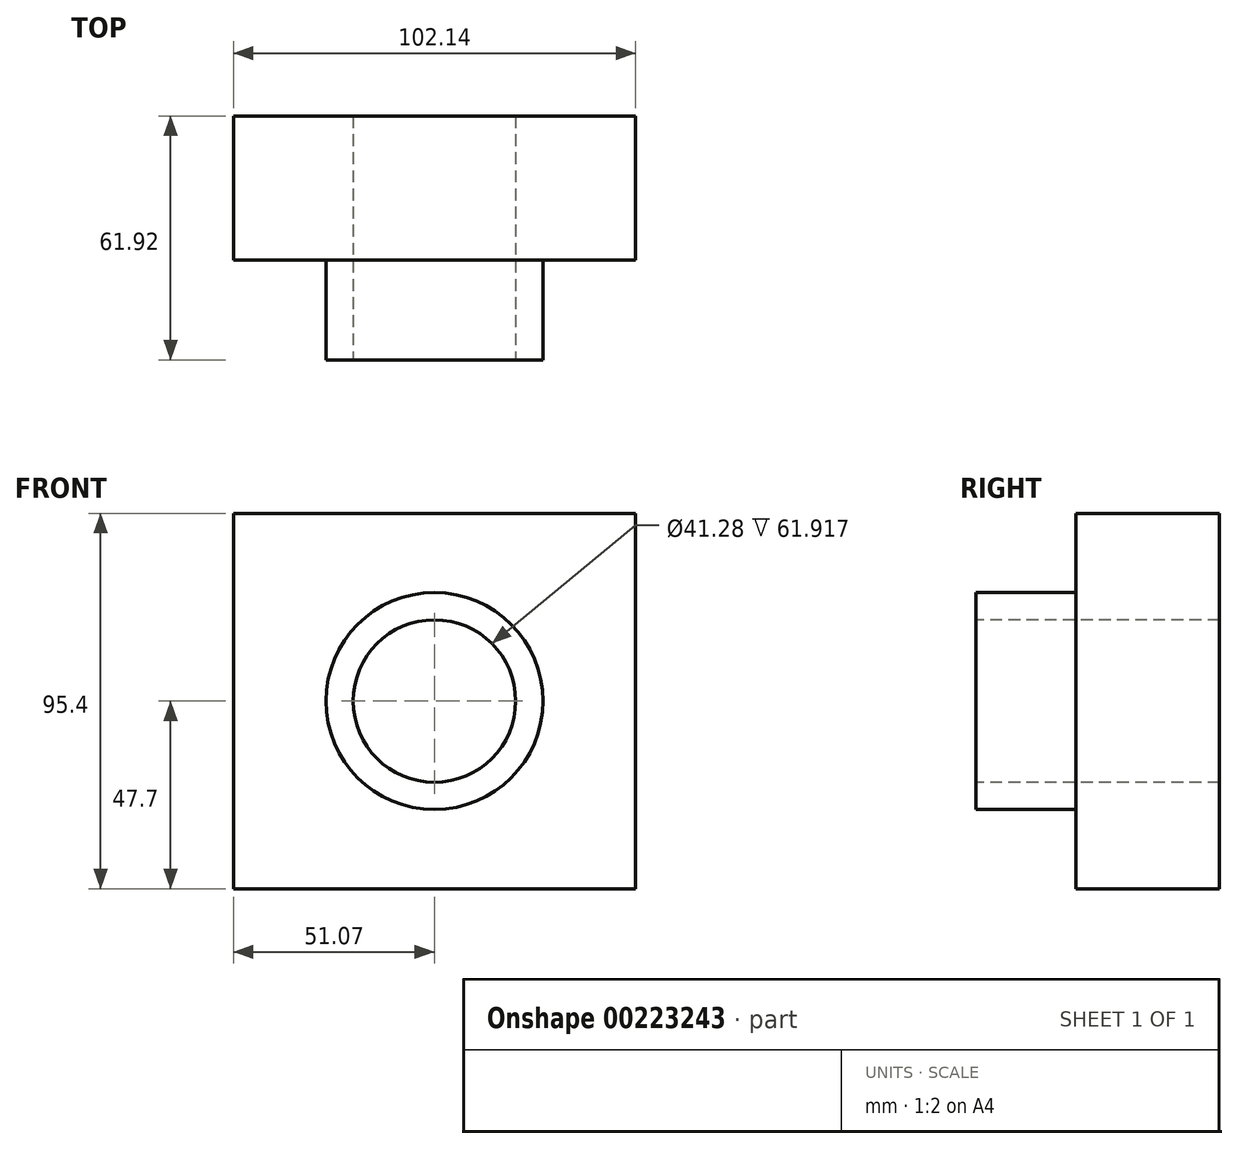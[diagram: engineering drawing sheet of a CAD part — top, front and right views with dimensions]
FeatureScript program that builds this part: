
annotation { "Feature Type Name" : "Feature", "Feature Type Description" : "" }
export const myFeature = defineFeature(function(context is Context, id is Id, definition is map)
    precondition{}
    {
        {
            var Q0;
            Q0=qCreatedBy(makeId("Front.planeOp"),FACE);
            var sketch = newSketch(context, id + "F0", { "sketchPlane" : qUnion([Q0])});
            skLineSegment(sketch, "E0.bottom", {"start": v(51.07, -47.7) * mm, "end": v(-51.07, -47.7) * mm});
            skLineSegment(sketch, "E0.top", {"start": v(51.07, 47.7) * mm, "end": v(-51.07, 47.7) * mm});
            skLineSegment(sketch, "E0.left", {"start": v(51.07, -47.7) * mm, "end": v(51.07, 47.7) * mm});
            skLineSegment(sketch, "E0.right", {"start": v(-51.07, -47.7) * mm, "end": v(-51.07, 47.7) * mm});
            skPoint(sketch, "E0.middle", {"position": v(0, 0) * mm});
            skSolve(sketch);
        }
        {
            var Q0;
            Q0 = qSketchRegion(id + "F0", true);
            extrude(context, id + "F1", {"entities" : qUnion([Q0]), "depth" : 25.4 * mm});
        }
        {
            var Q0;
            Q0=makeQuery(id+"F1.opExtrude","CAP_FACE",FACE,{"disambiguationData":[OSD([sQuery(id+"F0.wireOp",EDGE,"E0.bottom"),sQuery(id+"F0.wireOp",EDGE,"E0.top"),sQuery(id+"F0.wireOp",EDGE,"E0.left"),sQuery(id+"F0.wireOp",EDGE,"E0.right")])],"isStart":false});
            var sketch = newSketch(context, id + "F2", { "sketchPlane" : qUnion([Q0])});
            skCircle(sketch, "E1", {"center": v(0, 0) * mm, "radius": 27.56 * mm});
            skSolve(sketch);
        }
        {
            var Q0;
            Q0=makeQuery(id+"F2.imprint","IMPRINT",FACE,{"disambiguationData":[TD([[makeQuery(id+"F2.imprint","IMPRINT",EDGE,{"derivedFrom":sQuery(id+"F2.wireOp",EDGE,"E1")}),1.0]])]});
            extrude(context, id + "F4", {"entities" : qUnion([Q0]), "operationType" : NewBodyOperationType.ADD, "depth" : 25.4 * mm});
        }
        {
            var Q0;
            Q0=makeQuery(id+"F4.opExtrude","CAP_FACE",FACE,{"disambiguationData":[OSD([sQuery(id+"F2.wireOp",EDGE,"E1")])],"isStart":false});
            var sketch = newSketch(context, id + "F5", { "sketchPlane" : qUnion([Q0])});
            skCircle(sketch, "E2", {"center": v(0, 0) * mm, "radius": 20.64 * mm});
            skSolve(sketch);
        }
        {
            var Q0;
            Q0=makeQuery(id+"F5.imprint","IMPRINT",FACE,{"disambiguationData":[TD([[makeQuery(id+"F5.imprint","IMPRINT",EDGE,{"derivedFrom":sQuery(id+"F5.wireOp",EDGE,"E2")}),1.0]])]});
            extrude(context, id + "F6", {"entities" : qUnion([Q0]), "operationType" : NewBodyOperationType.REMOVE, "endBound" : BoundingType.THROUGH_ALL, "oppositeDirection" : true, "depth" : 25.4 * mm});
        }
        {
            var Q0;
            Q0=makeQuery(id+"F1.opExtrude","CAP_FACE",FACE,{"disambiguationData":[OSD([sQuery(id+"F0.wireOp",EDGE,"E0.bottom"),sQuery(id+"F0.wireOp",EDGE,"E0.top"),sQuery(id+"F0.wireOp",EDGE,"E0.left"),sQuery(id+"F0.wireOp",EDGE,"E0.right")])],"isStart":true});
            extrude(context, id + "F3", {"entities" : qUnion([Q0]), "operationType" : NewBodyOperationType.ADD, "depth" : 11.12 * mm});
        }
    });
